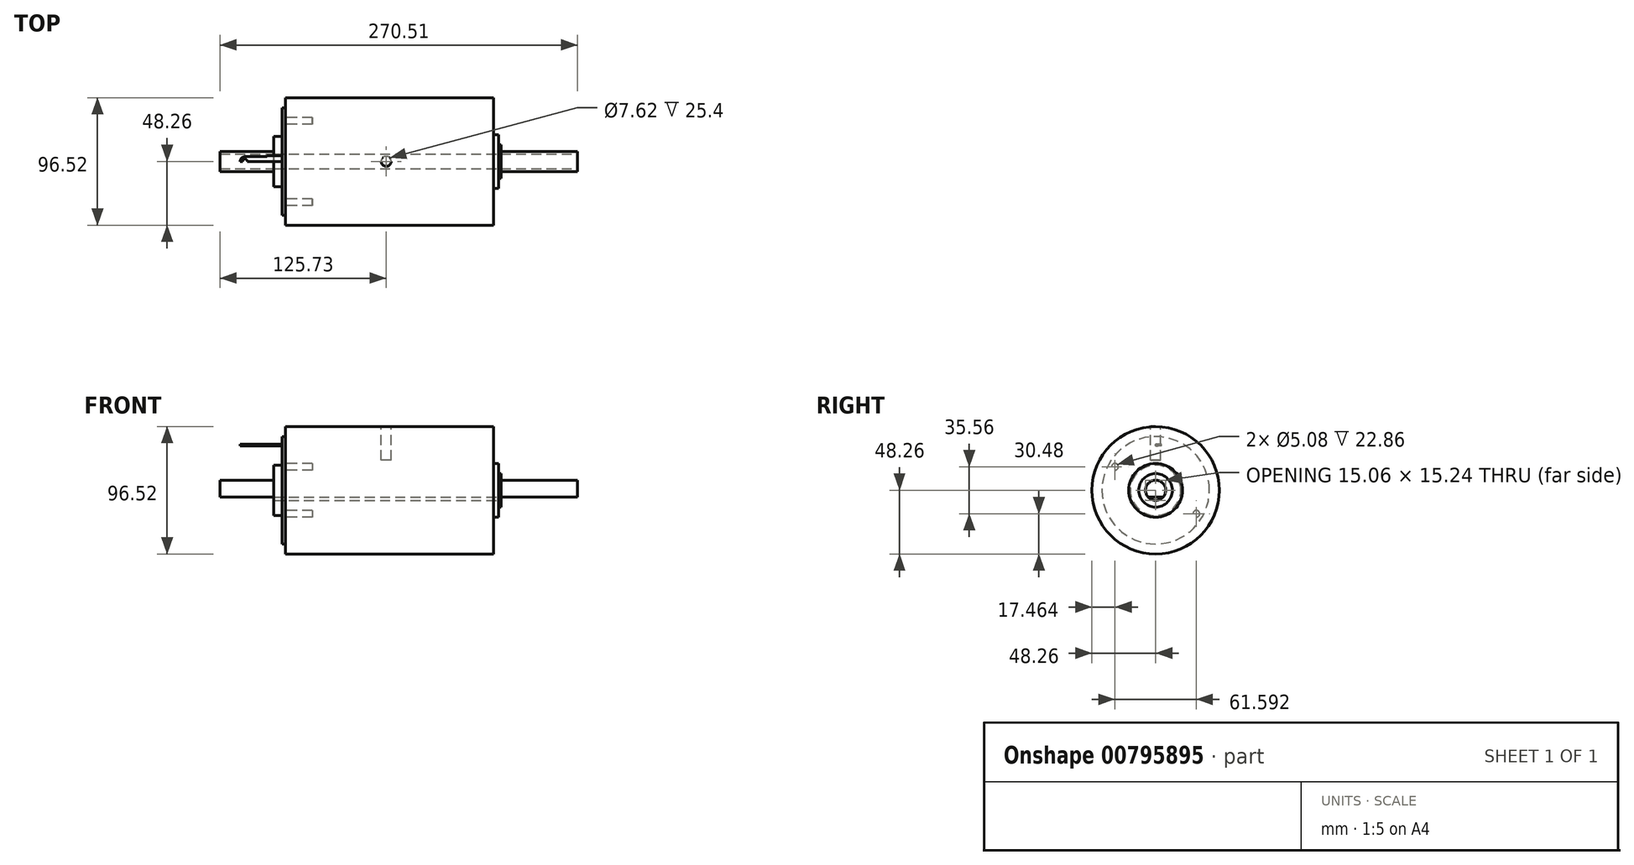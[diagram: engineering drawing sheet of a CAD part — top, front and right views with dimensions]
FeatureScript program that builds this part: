
annotation { "Feature Type Name" : "Feature", "Feature Type Description" : "" }
export const myFeature = defineFeature(function(context is Context, id is Id, definition is map)
    precondition{}
    {
        {
            var Q0;
            Q0=qCreatedBy(makeId("Front.planeOp"),FACE);
            var sketch = newSketch(context, id + "F0", { "sketchPlane" : qUnion([Q0])});
            skLineSegment(sketch, "E0", {"start": v(-276.23, 0) * mm, "end": v(14.9, 0) * mm, "construction": true});
            skLineSegment(sketch, "E1", {"start": v(0, 0) * mm, "end": v(0, 7.62) * mm});
            skLineSegment(sketch, "E2", {"start": v(0, 7.62) * mm, "end": v(-57.91, 7.62) * mm});
            skLineSegment(sketch, "E3", {"start": v(-57.91, 7.62) * mm, "end": v(-57.91, 12.7) * mm});
            skLineSegment(sketch, "E4", {"start": v(-57.91, 12.7) * mm, "end": v(-59.69, 12.7) * mm});
            skLineSegment(sketch, "E5", {"start": v(-59.69, 12.7) * mm, "end": v(-59.69, 20.32) * mm});
            skLineSegment(sketch, "E6", {"start": v(-59.69, 20.32) * mm, "end": v(-63.5, 20.32) * mm});
            skLineSegment(sketch, "E7", {"start": v(-63.5, 20.32) * mm, "end": v(-63.5, 48.26) * mm});
            skLineSegment(sketch, "E8", {"start": v(-63.5, 48.26) * mm, "end": v(-226.06, 48.26) * mm});
            skLineSegment(sketch, "E9", {"start": v(-226.06, 48.26) * mm, "end": v(-226.06, 19.05) * mm});
            skLineSegment(sketch, "E10", {"start": v(-226.06, 19.05) * mm, "end": v(-229.87, 19.05) * mm});
            skLineSegment(sketch, "E11", {"start": v(-229.87, 19.05) * mm, "end": v(-229.87, 7.62) * mm});
            skLineSegment(sketch, "E12", {"start": v(-229.87, 7.62) * mm, "end": v(-270.51, 7.62) * mm});
            skLineSegment(sketch, "E13", {"start": v(-270.51, 7.62) * mm, "end": v(-270.51, 0) * mm});
            skLineSegment(sketch, "E14", {"start": v(-270.51, 0) * mm, "end": v(0, 0) * mm});
            skSolve(sketch);
        }
        {
            var Q0;
            Q0 = qSketchRegion(id + "F0", true);
            var Q1;
            Q1=sQuery(id+"F0.wireOp",EDGE,"E0");
            revolve(context, id + "F1", {"surfaceOperationType" : NewSurfaceOperationType.NEW, "entities" : qUnion([Q0]), "axis" : qUnion([Q1]), "revolveType" : RevolveType.FULL});
        }
        {
            var Q0;
            Q0=qCreatedBy(makeId("Front.planeOp"),FACE);
            var sketch = newSketch(context, id + "F2", { "sketchPlane" : qUnion([Q0])});
            skLineSegment(sketch, "E15.bottom", {"start": v(-226.06, 34.92) * mm, "end": v(-265.67, 34.92) * mm});
            skLineSegment(sketch, "E15.top", {"start": v(-226.06, 33.65) * mm, "end": v(-265.67, 33.65) * mm});
            skLineSegment(sketch, "E15.left", {"start": v(-226.06, 34.92) * mm, "end": v(-226.06, 33.65) * mm});
            skLineSegment(sketch, "E15.right", {"start": v(-265.67, 34.92) * mm, "end": v(-265.67, 33.65) * mm});
            skSolve(sketch);
        }
        {
            var Q0;
            Q0=qCreatedBy(makeId("Top.planeOp"),FACE);
            cPlane(context, id + "F3", {"entities" : qUnion([Q0]), "cplaneType" : CPlaneType.OFFSET, "offset" : 34.92 * mm, "width" : 152.4 * mm, "height" : 152.4 * mm});
        }
        {
            var Q0;
            Q0=qCreatedBy(id+"F3.planeOp",FACE);
            var sketch = newSketch(context, id + "F4", { "sketchPlane" : qUnion([Q0])});
            skLineSegment(sketch, "E16", {"start": v(-226.06, 4.45) * mm, "end": v(-234.95, 4.45) * mm});
            skLineSegment(sketch, "E17", {"start": v(-234.95, 4.45) * mm, "end": v(-234.95, 3.56) * mm});
            skLineSegment(sketch, "E18", {"start": v(-234.95, 3.56) * mm, "end": v(-251.71, 3.56) * mm});
            skArc(sketch, "E19", {"start": v(-251.71, 3.56) * mm, "mid": v(-254.23, 2.51) * mm, "end": v(-255.27, 0) * mm});
            skArc(sketch, "E20", {"start": v(-249.94, 0) * mm, "mid": v(-251.71, 1.78) * mm, "end": v(-253.5, 0) * mm});
            skLineSegment(sketch, "E21", {"start": v(-226.06, 4.45) * mm, "end": v(-226.06, 0) * mm});
            skLineSegment(sketch, "E22", {"start": v(-226.06, 0) * mm, "end": v(-249.94, 0) * mm});
            skLineSegment(sketch, "E23.trimOffspring", {"start": v(-253.5, 0) * mm, "end": v(-255.27, 0) * mm});
            skSolve(sketch);
        }
        {
            var Q0;
            Q0 = qSketchRegion(id + "F4", true);
            extrude(context, id + "F5", {"entities" : qUnion([Q0]), "operationType" : NewBodyOperationType.ADD, "oppositeDirection" : true, "depth" : 1.27 * mm, "offsetDistance" : 25.4 * mm});
        }
        {
            var Q0;
            Q0=qCreatedBy(makeId("Top.planeOp"),FACE);
            cPlane(context, id + "F6", {"entities" : qUnion([Q0]), "cplaneType" : CPlaneType.OFFSET, "offset" : 48.26 * mm, "width" : 152.4 * mm, "height" : 152.4 * mm});
        }
        {
            var Q0;
            Q0=qCreatedBy(id+"F6.planeOp",FACE);
            var sketch = newSketch(context, id + "F7", { "sketchPlane" : qUnion([Q0])});
            skCircle(sketch, "E24", {"center": v(-144.78, 0) * mm, "radius": 3.8 * mm});
            skSolve(sketch);
        }
        {
            var Q0;
            Q0=makeQuery(id+"F7.imprint","IMPRINT",FACE,{"disambiguationData":[TD([[makeQuery(id+"F7.imprint","IMPRINT",EDGE,{"derivedFrom":sQuery(id+"F7.wireOp",EDGE,"E24")}),1.0]])]});
            extrude(context, id + "F8", {"entities" : qUnion([Q0]), "operationType" : NewBodyOperationType.REMOVE, "oppositeDirection" : true, "depth" : 25.4 * mm, "offsetDistance" : 25.4 * mm});
        }
        {
            var Q0;
            Q0=makeQuery(id+"F1.opRevolve","SWEPT_FACE",FACE,{"disambiguationData":[OSD([sQuery(id+"F0.wireOp",EDGE,"E9")])]});
            var sketch = newSketch(context, id + "F9", { "sketchPlane" : qUnion([Q0])});
            skCircle(sketch, "E25", {"center": v(0, 0) * mm, "radius": 35.56 * mm, "construction": true});
            skLineSegment(sketch, "E26", {"start": v(-50.47, -29.14) * mm, "end": v(50.68, 29.26) * mm, "construction": true});
            skLineSegment(sketch, "E27", {"start": v(0, 70) * mm, "end": v(0, -57.64) * mm, "construction": true});
            skLineSegment(sketch, "E28", {"start": v(63.42, 0) * mm, "end": v(-68.99, 0) * mm, "construction": true});
            skCircle(sketch, "E29", {"center": v(30.8, 17.78) * mm, "radius": 2.54 * mm});
            skCircle(sketch, "E30", {"center": v(-30.8, -17.78) * mm, "radius": 2.54 * mm});
            skCircle(sketch, "E31", {"center": v(0, 0) * mm, "radius": 40.64 * mm});
            skSolve(sketch);
        }
        {
            var Q0;
            Q0=makeQuery(id+"F9.imprint","IMPRINT",FACE,{"disambiguationData":[TD([[makeQuery(id+"F9.imprint","IMPRINT",EDGE,{"derivedFrom":sQuery(id+"F9.wireOp",EDGE,"E29")}),1.0]])]});
            var Q1;
            Q1=makeQuery(id+"F9.imprint","IMPRINT",FACE,{"disambiguationData":[TD([[makeQuery(id+"F9.imprint","IMPRINT",EDGE,{"derivedFrom":sQuery(id+"F9.wireOp",EDGE,"E30")}),1.0]])]});
            extrude(context, id + "F10", {"entities" : qUnion([Q0, Q1]), "operationType" : NewBodyOperationType.REMOVE, "oppositeDirection" : true, "depth" : 25.4 * mm, "offsetDistance" : 25.4 * mm});
        }
        {
            var Q0;
            Q0=makeQuery(id+"F9.imprint","IMPRINT",FACE,{"disambiguationData":[TD([[makeQuery(id+"F9.imprint","IMPRINT",EDGE,{"derivedFrom":sQuery(id+"F9.wireOp",EDGE,"E29")}),-1.0]])]});
            extrude(context, id + "F11", {"entities" : qUnion([Q0]), "operationType" : NewBodyOperationType.REMOVE, "oppositeDirection" : true, "depth" : 2.54 * mm, "offsetDistance" : 25.4 * mm});
        }
        {
            var Q0;
            Q0=makeQuery(id+"F9.imprint","IMPRINT",FACE,{"disambiguationData":[TD([[makeQuery(id+"F9.imprint","IMPRINT",EDGE,{"derivedFrom":sQuery(id+"F9.wireOp",EDGE,"E31")}),-1.0]])]});
            var sketch = newSketch(context, id + "F12", { "sketchPlane" : qUnion([Q0])});
            skSolve(sketch);
        }
        {
            var Q0;
            Q0=makeQuery(id+"F12.imprint","IMPRINT",FACE,{"disambiguationData":[TD([[makeQuery(id+"F12.imprint","IMPRINT",EDGE,{"derivedFrom":makeQuery(id+"F9.imprint","IMPRINT",EDGE,{"derivedFrom":sQuery(id+"F9.wireOp",EDGE,"E31")})}),-1.0]])]});
            extrude(context, id + "F13", {"entities" : qUnion([Q0]), "operationType" : NewBodyOperationType.REMOVE, "oppositeDirection" : true, "depth" : 5.08 * mm, "offsetDistance" : 25.4 * mm});
        }
        {
            var Q0;
            Q0=makeQuery(id+"F1.opRevolve","SWEPT_FACE",FACE,{"disambiguationData":[OSD([sQuery(id+"F0.wireOp",EDGE,"E1")])]});
            var sketch = newSketch(context, id + "F14", { "sketchPlane" : qUnion([Q0])});
            skCircle(sketch, "E32.0", {"center": v(0, 0) * mm, "radius": 7.62 * mm});
            skLineSegment(sketch, "E33", {"start": v(5.68, -5.08) * mm, "end": v(-5.68, -5.08) * mm});
            skSolve(sketch);
        }
        {
            var Q0;
            {var subQ0=sQuery(id+"F14.wireOp",EDGE,"E33");Q0=makeQuery(id+"F14.imprint","IMPRINT",FACE,{"disambiguationData":[TD([[makeQuery(id+"F14.imprint","IMPRINT",EDGE,{"derivedFrom":subQ0}),1.0]])]});}
            extrude(context, id + "F15", {"entities" : qUnion([Q0]), "operationType" : NewBodyOperationType.REMOVE, "endBound" : BoundingType.UP_TO_NEXT, "oppositeDirection" : true, "depth" : 25.4 * mm, "offsetDistance" : 25.4 * mm});
        }
    });
